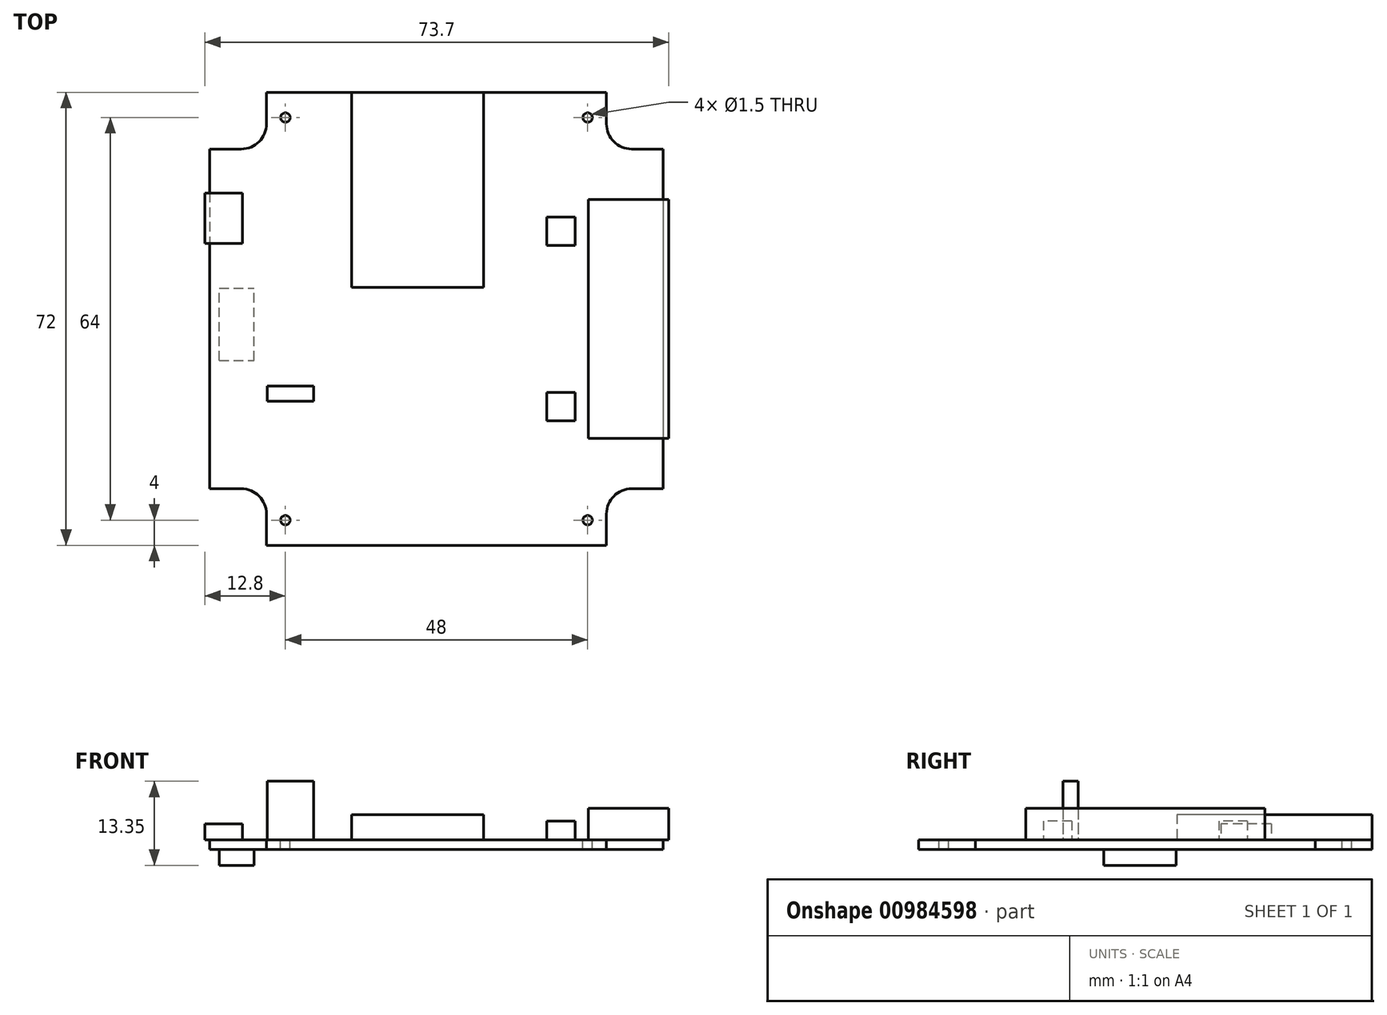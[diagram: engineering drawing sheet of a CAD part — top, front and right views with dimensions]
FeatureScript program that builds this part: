
annotation { "Feature Type Name" : "Feature", "Feature Type Description" : "" }
export const myFeature = defineFeature(function(context is Context, id is Id, definition is map)
    precondition{}
    {
        {
            var Q0;
            Q0=qCreatedBy(makeId("Top.planeOp"),FACE);
            var sketch = newSketch(context, id + "F0", { "sketchPlane" : qUnion([Q0])});
            skLineSegment(sketch, "E0.bottom", {"start": v(0, 0) * mm, "end": v(-72, 0) * mm});
            skLineSegment(sketch, "E0.top", {"start": v(0, -72) * mm, "end": v(-72, -72) * mm});
            skLineSegment(sketch, "E0.left", {"start": v(0, 0) * mm, "end": v(0, -72) * mm});
            skLineSegment(sketch, "E0.right", {"start": v(-72, 0) * mm, "end": v(-72, -72) * mm});
            skSolve(sketch);
        }
        {
            var Q0;
            Q0 = qSketchRegion(id + "F0", true);
            extrude(context, id + "F1", {"entities" : qUnion([Q0]), "oppositeDirection" : true, "depth" : 1.55 * mm, "offsetDistance" : 25 * mm});
        }
        {
            var Q0;
            Q0=makeQuery(id+"F1.opExtrude","CAP_FACE",FACE,{"disambiguationData":[OSD([sQuery(id+"F0.wireOp",EDGE,"E0.bottom"),sQuery(id+"F0.wireOp",EDGE,"E0.top"),sQuery(id+"F0.wireOp",EDGE,"E0.left"),sQuery(id+"F0.wireOp",EDGE,"E0.right")])],"isStart":true});
            var sketch = newSketch(context, id + "F2", { "sketchPlane" : qUnion([Q0])});
            skLineSegment(sketch, "E1.bottom", {"start": v(0, -72) * mm, "end": v(-9, -72) * mm});
            skLineSegment(sketch, "E1.top", {"start": v(0, -63) * mm, "end": v(-9, -63) * mm});
            skLineSegment(sketch, "E1.left", {"start": v(0, -72) * mm, "end": v(0, -63) * mm});
            skLineSegment(sketch, "E1.right", {"start": v(-9, -72) * mm, "end": v(-9, -63) * mm});
            skLineSegment(sketch, "E2.bottom", {"start": v(-72, -72) * mm, "end": v(-63, -72) * mm});
            skLineSegment(sketch, "E2.top", {"start": v(-72, -63) * mm, "end": v(-63, -63) * mm});
            skLineSegment(sketch, "E2.left", {"start": v(-72, -72) * mm, "end": v(-72, -63) * mm});
            skLineSegment(sketch, "E2.right", {"start": v(-63, -72) * mm, "end": v(-63, -63) * mm});
            skLineSegment(sketch, "E3.bottom", {"start": v(-72, 0) * mm, "end": v(-63, 0) * mm});
            skLineSegment(sketch, "E3.top", {"start": v(-72, -9) * mm, "end": v(-63, -9) * mm});
            skLineSegment(sketch, "E3.left", {"start": v(-72, 0) * mm, "end": v(-72, -9) * mm});
            skLineSegment(sketch, "E3.right", {"start": v(-63, 0) * mm, "end": v(-63, -9) * mm});
            skLineSegment(sketch, "E4.bottom", {"start": v(0, 0) * mm, "end": v(-9, 0) * mm});
            skLineSegment(sketch, "E4.top", {"start": v(0, -9) * mm, "end": v(-9, -9) * mm});
            skLineSegment(sketch, "E4.left", {"start": v(0, 0) * mm, "end": v(0, -9) * mm});
            skLineSegment(sketch, "E4.right", {"start": v(-9, 0) * mm, "end": v(-9, -9) * mm});
            skSolve(sketch);
        }
        {
            var Q0;
            Q0=makeQuery(id+"F2.imprint","IMPRINT",FACE,{"disambiguationData":[TD([[makeQuery(id+"F2.imprint","IMPRINT",EDGE,{"derivedFrom":sQuery(id+"F2.wireOp",EDGE,"E2.bottom")}),-1.0]])]});
            var Q1;
            Q1=makeQuery(id+"F2.imprint","IMPRINT",FACE,{"disambiguationData":[TD([[makeQuery(id+"F2.imprint","IMPRINT",EDGE,{"derivedFrom":sQuery(id+"F2.wireOp",EDGE,"E3.bottom")}),1.0]])]});
            var Q2;
            Q2=makeQuery(id+"F2.imprint","IMPRINT",FACE,{"disambiguationData":[TD([[makeQuery(id+"F2.imprint","IMPRINT",EDGE,{"derivedFrom":sQuery(id+"F2.wireOp",EDGE,"E4.bottom")}),1.0]])]});
            var Q3;
            Q3=makeQuery(id+"F2.imprint","IMPRINT",FACE,{"disambiguationData":[TD([[makeQuery(id+"F2.imprint","IMPRINT",EDGE,{"derivedFrom":sQuery(id+"F2.wireOp",EDGE,"E1.bottom")}),-1.0]])]});
            extrude(context, id + "F3", {"entities" : qUnion([Q0, Q1, Q2, Q3]), "operationType" : NewBodyOperationType.REMOVE, "endBound" : BoundingType.THROUGH_ALL, "oppositeDirection" : true, "depth" : 25 * mm, "offsetDistance" : 25 * mm});
        }
        {
            var Q0;
            Q0=makeQuery(id+"F3.boolean.opBoolean","COPY",EDGE,{"derivedFrom":makeQuery(id+"F3.opExtrude","SWEPT_EDGE",EDGE,{"disambiguationData":[OSD([sQuery(id+"F2.wireOp",EDGE,"E1.top"),sQuery(id+"F2.wireOp",EDGE,"E1.right")])]})});
            var Q1;
            Q1=makeQuery(id+"F3.boolean.opBoolean","COPY",EDGE,{"derivedFrom":makeQuery(id+"F3.opExtrude","SWEPT_EDGE",EDGE,{"disambiguationData":[OSD([sQuery(id+"F2.wireOp",EDGE,"E2.top"),sQuery(id+"F2.wireOp",EDGE,"E2.right")])]})});
            var Q2;
            Q2=makeQuery(id+"F3.boolean.opBoolean","COPY",EDGE,{"derivedFrom":makeQuery(id+"F3.opExtrude","SWEPT_EDGE",EDGE,{"disambiguationData":[OSD([sQuery(id+"F2.wireOp",EDGE,"E3.top"),sQuery(id+"F2.wireOp",EDGE,"E3.right")])]})});
            var Q3;
            Q3=makeQuery(id+"F3.boolean.opBoolean","COPY",EDGE,{"derivedFrom":makeQuery(id+"F3.opExtrude","SWEPT_EDGE",EDGE,{"disambiguationData":[OSD([sQuery(id+"F2.wireOp",EDGE,"E4.top"),sQuery(id+"F2.wireOp",EDGE,"E4.right")])]})});
            fillet(context, id + "F4", {"entities" : qUnion([Q0, Q1, Q2, Q3]), "radius" : 4 * mm, "tangentPropagation" : true, "allowEdgeOverflow" : false});
        }
        {
            var Q0;
            Q0=makeQuery(id+"F1.opExtrude","CAP_FACE",FACE,{"disambiguationData":[OSD([sQuery(id+"F0.wireOp",EDGE,"E0.bottom"),sQuery(id+"F0.wireOp",EDGE,"E0.top"),sQuery(id+"F0.wireOp",EDGE,"E0.left"),sQuery(id+"F0.wireOp",EDGE,"E0.right")])],"isStart":true});
            var sketch = newSketch(context, id + "F5", { "sketchPlane" : qUnion([Q0])});
            skLineSegment(sketch, "E5.bottom", {"start": v(-49.5, 0) * mm, "end": v(-28.5, 0) * mm});
            skLineSegment(sketch, "E5.top", {"start": v(-49.5, -31) * mm, "end": v(-28.5, -31) * mm});
            skLineSegment(sketch, "E5.left", {"start": v(-49.5, 0) * mm, "end": v(-49.5, -31) * mm});
            skLineSegment(sketch, "E5.right", {"start": v(-28.5, 0) * mm, "end": v(-28.5, -31) * mm});
            skSolve(sketch);
        }
        {
            var Q0;
            Q0=makeQuery(id+"F5.imprint","IMPRINT",FACE,{"disambiguationData":[TD([[makeQuery(id+"F5.imprint","IMPRINT",EDGE,{"derivedFrom":sQuery(id+"F5.wireOp",EDGE,"E5.bottom")}),1.0]])]});
            extrude(context, id + "F6", {"entities" : qUnion([Q0]), "operationType" : NewBodyOperationType.ADD, "depth" : 4 * mm, "offsetDistance" : 25 * mm});
        }
        {
            var Q0;
            Q0=makeQuery(id+"F1.opExtrude","CAP_FACE",FACE,{"disambiguationData":[OSD([sQuery(id+"F0.wireOp",EDGE,"E0.bottom"),sQuery(id+"F0.wireOp",EDGE,"E0.top"),sQuery(id+"F0.wireOp",EDGE,"E0.left"),sQuery(id+"F0.wireOp",EDGE,"E0.right")])],"isStart":true});
            var sketch = newSketch(context, id + "F7", { "sketchPlane" : qUnion([Q0])});
            skLineSegment(sketch, "E6.bottom", {"start": v(-72.8, -16) * mm, "end": v(-66.8, -16) * mm});
            skLineSegment(sketch, "E6.top", {"start": v(-72.8, -24) * mm, "end": v(-66.8, -24) * mm});
            skLineSegment(sketch, "E6.left", {"start": v(-72.8, -16) * mm, "end": v(-72.8, -24) * mm});
            skLineSegment(sketch, "E6.right", {"start": v(-66.8, -16) * mm, "end": v(-66.8, -24) * mm});
            skSolve(sketch);
        }
        {
            var Q0;
            {var subQ0=sQuery(id+"F7.wireOp",EDGE,"E6.right");Q0=makeQuery(id+"F7.imprint","IMPRINT",FACE,{"disambiguationData":[TD([[makeQuery(id+"F7.imprint","IMPRINT",EDGE,{"derivedFrom":subQ0}),-1.0]])]});}
            var Q1;
            {var subQ0=sQuery(id+"F7.wireOp",EDGE,"E6.left");Q1=makeQuery(id+"F7.imprint","IMPRINT",FACE,{"disambiguationData":[TD([[makeQuery(id+"F7.imprint","IMPRINT",EDGE,{"derivedFrom":subQ0}),1.0]])]});}
            extrude(context, id + "F8", {"entities" : qUnion([Q0, Q1]), "operationType" : NewBodyOperationType.ADD, "depth" : 2.5 * mm, "offsetDistance" : 25 * mm});
        }
        {
            var Q0;
            Q0=makeQuery(id+"F1.opExtrude","CAP_FACE",FACE,{"disambiguationData":[OSD([sQuery(id+"F0.wireOp",EDGE,"E0.bottom"),sQuery(id+"F0.wireOp",EDGE,"E0.top"),sQuery(id+"F0.wireOp",EDGE,"E0.left"),sQuery(id+"F0.wireOp",EDGE,"E0.right")])],"isStart":true});
            var sketch = newSketch(context, id + "F9", { "sketchPlane" : qUnion([Q0])});
            skLineSegment(sketch, "E7.bottom", {"start": v(-11.9, -17) * mm, "end": v(0.9, -17) * mm});
            skLineSegment(sketch, "E7.top", {"start": v(-11.9, -55) * mm, "end": v(0.9, -55) * mm});
            skLineSegment(sketch, "E7.left", {"start": v(-11.9, -17) * mm, "end": v(-11.9, -55) * mm});
            skLineSegment(sketch, "E7.right", {"start": v(0.9, -17) * mm, "end": v(0.9, -55) * mm});
            skLineSegment(sketch, "E8", {"start": v(-9, 0) * mm, "end": v(-9, -17) * mm, "construction": true});
            skPoint(sketch, "E8.endSnap0", {"position": v(-5.5, -17) * mm});
            skLineSegment(sketch, "E9", {"start": v(-9, -72) * mm, "end": v(-9, -55) * mm, "construction": true});
            skSolve(sketch);
        }
        {
            var Q0;
            Q0 = qSketchRegion(id + "F9", true);
            extrude(context, id + "F10", {"entities" : qUnion([Q0]), "operationType" : NewBodyOperationType.ADD, "depth" : 5 * mm, "offsetDistance" : 25 * mm});
        }
        {
            var Q0;
            Q0=makeQuery(id+"F1.opExtrude","CAP_FACE",FACE,{"disambiguationData":[OSD([sQuery(id+"F0.wireOp",EDGE,"E0.bottom"),sQuery(id+"F0.wireOp",EDGE,"E0.top"),sQuery(id+"F0.wireOp",EDGE,"E0.left"),sQuery(id+"F0.wireOp",EDGE,"E0.right")])],"isStart":false});
            var sketch = newSketch(context, id + "F11", { "sketchPlane" : qUnion([Q0])});
            skLineSegment(sketch, "E10.bottom", {"start": v(-70.5, 42.6) * mm, "end": v(-65, 42.6) * mm});
            skLineSegment(sketch, "E10.top", {"start": v(-70.5, 31.1) * mm, "end": v(-65, 31.1) * mm});
            skLineSegment(sketch, "E10.left", {"start": v(-70.5, 42.6) * mm, "end": v(-70.5, 31.1) * mm});
            skLineSegment(sketch, "E10.right", {"start": v(-65, 42.6) * mm, "end": v(-65, 31.1) * mm});
            skSolve(sketch);
        }
        {
            var Q0;
            Q0=makeQuery(id+"F11.imprint","IMPRINT",FACE,{"disambiguationData":[TD([[makeQuery(id+"F11.imprint","IMPRINT",EDGE,{"derivedFrom":sQuery(id+"F11.wireOp",EDGE,"E10.bottom")}),-1.0]])]});
            extrude(context, id + "F12", {"entities" : qUnion([Q0]), "operationType" : NewBodyOperationType.ADD, "depth" : 2.5 * mm, "offsetDistance" : 25 * mm});
        }
        {
            var Q0;
            Q0=makeQuery(id+"F1.opExtrude","CAP_FACE",FACE,{"disambiguationData":[OSD([sQuery(id+"F0.wireOp",EDGE,"E0.bottom"),sQuery(id+"F0.wireOp",EDGE,"E0.top"),sQuery(id+"F0.wireOp",EDGE,"E0.left"),sQuery(id+"F0.wireOp",EDGE,"E0.right")])],"isStart":true});
            var sketch = newSketch(context, id + "F13", { "sketchPlane" : qUnion([Q0])});
            skLineSegment(sketch, "E11.bottom", {"start": v(-60, -4) * mm, "end": v(-12, -4) * mm, "construction": true});
            skLineSegment(sketch, "E11.top", {"start": v(-60, -68) * mm, "end": v(-12, -68) * mm, "construction": true});
            skLineSegment(sketch, "E11.left", {"start": v(-60, -4) * mm, "end": v(-60, -68) * mm, "construction": true});
            skLineSegment(sketch, "E11.right", {"start": v(-12, -4) * mm, "end": v(-12, -68) * mm, "construction": true});
            skLineSegment(sketch, "E12", {"start": v(-52.5, -4) * mm, "end": v(-52.5, 0) * mm, "construction": true});
            skLineSegment(sketch, "E13", {"start": v(-51.14, -68) * mm, "end": v(-51.14, -72) * mm, "construction": true});
            skLineSegment(sketch, "E14", {"start": v(-60, -44.52) * mm, "end": v(-72, -44.52) * mm, "construction": true});
            skLineSegment(sketch, "E15", {"start": v(-12, -59.68) * mm, "end": v(0, -59.68) * mm, "construction": true});
            skCircle(sketch, "E16", {"center": v(-60, -4) * mm, "radius": 0.75 * mm});
            skCircle(sketch, "E17", {"center": v(-12, -4) * mm, "radius": 0.75 * mm});
            skCircle(sketch, "E18", {"center": v(-12, -68) * mm, "radius": 0.75 * mm});
            skCircle(sketch, "E19", {"center": v(-60, -68) * mm, "radius": 0.75 * mm});
            skSolve(sketch);
        }
        {
            var Q0;
            Q0 = qSketchRegion(id + "F13", true);
            extrude(context, id + "F14", {"entities" : qUnion([Q0]), "operationType" : NewBodyOperationType.REMOVE, "endBound" : BoundingType.THROUGH_ALL, "oppositeDirection" : true, "depth" : 25 * mm, "offsetDistance" : 25 * mm});
        }
        {
            var Q0;
            Q0=makeQuery(id+"F1.opExtrude","CAP_FACE",FACE,{"disambiguationData":[OSD([sQuery(id+"F0.wireOp",EDGE,"E0.bottom"),sQuery(id+"F0.wireOp",EDGE,"E0.top"),sQuery(id+"F0.wireOp",EDGE,"E0.left"),sQuery(id+"F0.wireOp",EDGE,"E0.right")])],"isStart":true});
            var sketch = newSketch(context, id + "F15", { "sketchPlane" : qUnion([Q0])});
            skLineSegment(sketch, "E20.bottom", {"start": v(-18.5, -19.8) * mm, "end": v(-14, -19.8) * mm});
            skLineSegment(sketch, "E20.top", {"start": v(-18.5, -24.3) * mm, "end": v(-14, -24.3) * mm});
            skLineSegment(sketch, "E20.left", {"start": v(-18.5, -19.8) * mm, "end": v(-18.5, -24.3) * mm});
            skLineSegment(sketch, "E20.right", {"start": v(-14, -19.8) * mm, "end": v(-14, -24.3) * mm});
            skLineSegment(sketch, "E21", {"start": v(-14, 0) * mm, "end": v(-14, -72) * mm, "construction": true});
            skLineSegment(sketch, "E22.bottom", {"start": v(-14, -47.7) * mm, "end": v(-18.5, -47.7) * mm});
            skLineSegment(sketch, "E22.top", {"start": v(-14, -52.2) * mm, "end": v(-18.5, -52.2) * mm});
            skLineSegment(sketch, "E22.left", {"start": v(-14, -47.7) * mm, "end": v(-14, -52.2) * mm});
            skLineSegment(sketch, "E22.right", {"start": v(-18.5, -47.7) * mm, "end": v(-18.5, -52.2) * mm});
            skLineSegment(sketch, "E23", {"start": v(-16.25, -19.8) * mm, "end": v(-16.25, 0) * mm, "construction": true});
            skLineSegment(sketch, "E24", {"start": v(-16.25, -52.2) * mm, "end": v(-16.25, -72) * mm, "construction": true});
            skSolve(sketch);
        }
        {
            var Q0;
            Q0=makeQuery(id+"F15.imprint","IMPRINT",FACE,{"disambiguationData":[TD([[makeQuery(id+"F15.imprint","IMPRINT",EDGE,{"derivedFrom":sQuery(id+"F15.wireOp",EDGE,"E20.bottom")}),-1.0]])]});
            var Q1;
            Q1=makeQuery(id+"F15.imprint","IMPRINT",FACE,{"disambiguationData":[TD([[makeQuery(id+"F15.imprint","IMPRINT",EDGE,{"derivedFrom":sQuery(id+"F15.wireOp",EDGE,"E22.bottom")}),1.0]])]});
            extrude(context, id + "F16", {"entities" : qUnion([Q0, Q1]), "operationType" : NewBodyOperationType.ADD, "depth" : 3 * mm, "offsetDistance" : 25 * mm});
        }
        {
            var Q0;
            Q0=makeQuery(id+"F1.opExtrude","CAP_FACE",FACE,{"disambiguationData":[OSD([sQuery(id+"F0.wireOp",EDGE,"E0.bottom"),sQuery(id+"F0.wireOp",EDGE,"E0.top"),sQuery(id+"F0.wireOp",EDGE,"E0.left"),sQuery(id+"F0.wireOp",EDGE,"E0.right")])],"isStart":true});
            var sketch = newSketch(context, id + "F17", { "sketchPlane" : qUnion([Q0])});
            skLineSegment(sketch, "E25.bottom", {"start": v(-62.9, -46.7) * mm, "end": v(-55.5, -46.7) * mm});
            skLineSegment(sketch, "E25.top", {"start": v(-62.9, -49.1) * mm, "end": v(-55.5, -49.1) * mm});
            skLineSegment(sketch, "E25.left", {"start": v(-62.9, -46.7) * mm, "end": v(-62.9, -49.1) * mm});
            skLineSegment(sketch, "E25.right", {"start": v(-55.5, -46.7) * mm, "end": v(-55.5, -49.1) * mm});
            skSolve(sketch);
        }
        {
            var Q0;
            Q0=makeQuery(id+"F17.imprint","IMPRINT",FACE,{"disambiguationData":[TD([[makeQuery(id+"F17.imprint","IMPRINT",EDGE,{"derivedFrom":sQuery(id+"F17.wireOp",EDGE,"E25.bottom")}),-1.0]])]});
            extrude(context, id + "F18", {"entities" : qUnion([Q0]), "operationType" : NewBodyOperationType.ADD, "depth" : 9.3 * mm, "offsetDistance" : 25 * mm});
        }
    });
